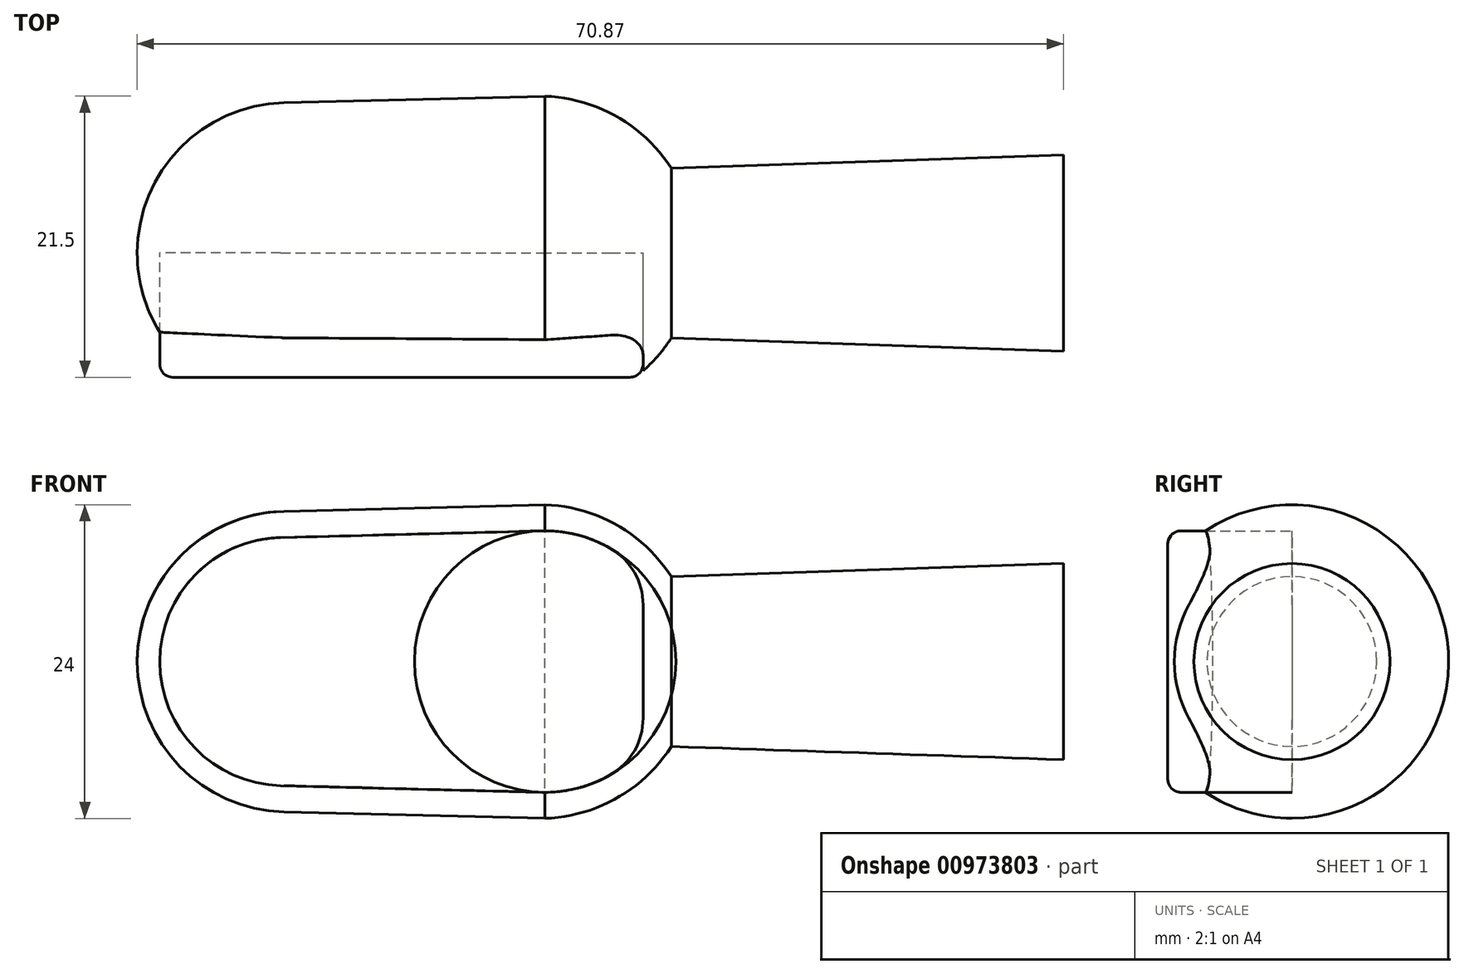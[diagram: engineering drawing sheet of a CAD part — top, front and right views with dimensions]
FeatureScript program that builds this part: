
annotation { "Feature Type Name" : "Feature", "Feature Type Description" : "" }
export const myFeature = defineFeature(function(context is Context, id is Id, definition is map)
    precondition{}
    {
        {
            var Q0;
            Q0=qCreatedBy(makeId("Right.planeOp"),FACE);
            var sketch = newSketch(context, id + "F0", { "sketchPlane" : qUnion([Q0])});
            skCircle(sketch, "E0", {"center": v(0, 0) * mm, "radius": 7.5 * mm});
            skSolve(sketch);
        }
        {
            var Q0;
            Q0=qCreatedBy(makeId("Right.planeOp"),FACE);
            cPlane(context, id + "F1", {"entities" : qUnion([Q0]), "cplaneType" : CPlaneType.OFFSET, "offset" : 30 * mm, "oppositeDirection" : true, "width" : 150 * mm, "height" : 150 * mm});
        }
        {
            var Q0;
            Q0=qCreatedBy(id+"F1.planeOp",FACE);
            var sketch = newSketch(context, id + "F2", { "sketchPlane" : qUnion([Q0])});
            skCircle(sketch, "E1", {"center": v(0, 0) * mm, "radius": 6.5 * mm});
            skSolve(sketch);
        }
        {
            var Q0;
            Q0=makeQuery(id+"F0.imprint","IMPRINT",FACE,{"disambiguationData":[TD([[makeQuery(id+"F0.imprint","IMPRINT",EDGE,{"derivedFrom":sQuery(id+"F0.wireOp",EDGE,"E0")}),1.0]])]});
            var Q1;
            Q1=makeQuery(id+"F2.imprint","IMPRINT",FACE,{"disambiguationData":[TD([[makeQuery(id+"F2.imprint","IMPRINT",EDGE,{"derivedFrom":sQuery(id+"F2.wireOp",EDGE,"E1")}),1.0]])]});
            loft(context, id + "F3", {"sheetProfilesArray" : [{ "sheetProfileEntities" : qUnion([Q0]) }, { "sheetProfileEntities" : qUnion([Q1]) }]});
        }
        {
            var Q0;
            Q0=qCreatedBy(makeId("Front.planeOp"),FACE);
            var sketch = newSketch(context, id + "F4", { "sketchPlane" : qUnion([Q0])});
            skLineSegment(sketch, "E2", {"start": v(0, 0) * mm, "end": v(-30, 0) * mm, "construction": true});
            skLineSegment(sketch, "E3", {"start": v(-30, 0) * mm, "end": v(-39.37, 0) * mm, "construction": true});
            skLineSegment(sketch, "E4", {"start": v(-39.37, 0) * mm, "end": v(-59.37, 0) * mm, "construction": true});
            skArc(sketch, "E5", {"start": v(-59.65, 11.5) * mm, "mid": v(-67.6, 8.03) * mm, "end": v(-70.87, 0) * mm});
            skLineSegment(sketch, "E6", {"start": v(-30, 0) * mm, "end": v(-30, 6.5) * mm});
            skPoint(sketch, "E7", {"position": v(-30, 6.5) * mm});
            skLineSegment(sketch, "E8", {"start": v(-59.65, 11.5) * mm, "end": v(-39.67, 12) * mm});
            skArc(sketch, "E9.trimOffspring", {"start": v(-30, 6.5) * mm, "mid": v(-34.16, 10.44) * mm, "end": v(-39.67, 12) * mm});
            skPoint(sketch, "E10", {"position": v(-30, -7.5) * mm});
            skLineSegment(sketch, "E11", {"start": v(-70.87, 0) * mm, "end": v(-30, 0) * mm});
            skPoint(sketch, "E12", {"position": v(-70.87, 0) * mm});
            skSolve(sketch);
        }
        {
            var Q0;
            Q0=makeQuery(id+"F4.imprint","IMPRINT",FACE,{"disambiguationData":[TD([[makeQuery(id+"F4.imprint","IMPRINT",EDGE,{"derivedFrom":sQuery(id+"F4.wireOp",EDGE,"E5")}),1.0]])]});
            var Q1;
            Q1=sQuery(id+"F4.wireOp",EDGE,"E4");
            revolve(context, id + "F5", {"operationType" : NewBodyOperationType.ADD, "surfaceOperationType" : NewSurfaceOperationType.NEW, "entities" : qUnion([Q0]), "axis" : qUnion([Q1]), "revolveType" : RevolveType.FULL});
        }
        {
            var Q0;
            Q0=qCreatedBy(makeId("Front.planeOp"),FACE);
            var sketch = newSketch(context, id + "F6", { "sketchPlane" : qUnion([Q0])});
            skLineSegment(sketch, "E13", {"start": v(0, 0) * mm, "end": v(-39.65, 0) * mm, "construction": true});
            skLineSegment(sketch, "E14", {"start": v(-39.65, 0) * mm, "end": v(-59.65, 0) * mm, "construction": true});
            skArc(sketch, "E15", {"start": v(-59.9, 9.49) * mm, "mid": v(-69.14, 0) * mm, "end": v(-59.9, -9.49) * mm});
            skArc(sketch, "E16", {"start": v(-39.9, -10) * mm, "mid": v(-37.19, -9.7) * mm, "end": v(-34.65, -8.66) * mm});
            skLineSegment(sketch, "E17", {"start": v(-59.9, 9.49) * mm, "end": v(-39.9, 10) * mm});
            skLineSegment(sketch, "E18", {"start": v(-39.9, -10) * mm, "end": v(-59.9, -9.49) * mm});
            skLineSegment(sketch, "E19", {"start": v(-32.15, 4.33) * mm, "end": v(-32.15, -4.33) * mm});
            skArc(sketch, "E20.trimOffspring", {"start": v(-34.65, 8.66) * mm, "mid": v(-37.19, 9.7) * mm, "end": v(-39.9, 10) * mm});
            skPoint(sketch, "E21.visualSharp", {"position": v(-32.15, 6.61) * mm});
            skArc(sketch, "E21.filletArc", {"start": v(-32.15, 4.33) * mm, "mid": v(-32.82, 6.83) * mm, "end": v(-34.65, 8.66) * mm});
            skPoint(sketch, "E22.visualSharp", {"position": v(-32.15, -6.61) * mm});
            skArc(sketch, "E22.filletArc", {"start": v(-34.65, -8.66) * mm, "mid": v(-32.82, -6.83) * mm, "end": v(-32.15, -4.33) * mm});
            skLineSegment(sketch, "E23", {"start": v(-39.67, 12) * mm, "end": v(-59.64, 11.49) * mm, "construction": true});
            skLineSegment(sketch, "E24", {"start": v(0, 0) * mm, "end": v(0, 12) * mm, "construction": true});
            skLineSegment(sketch, "E25", {"start": v(0, 12) * mm, "end": v(-39.67, 12) * mm, "construction": true});
            skSolve(sketch);
        }
        {
            var Q0;
            Q0 = qSketchRegion(id + "F6", true);
            extrude(context, id + "F7", {"entities" : qUnion([Q0]), "operationType" : NewBodyOperationType.REMOVE, "depth" : 15 * mm, "offsetDistance" : 25 * mm});
        }
        {
            var Q0;
            Q0=qCreatedBy(makeId("Front.planeOp"),FACE);
            var sketch = newSketch(context, id + "F8", { "sketchPlane" : qUnion([Q0])});
            skLineSegment(sketch, "E26", {"start": v(0, 0) * mm, "end": v(-39.65, 0) * mm, "construction": true});
            skLineSegment(sketch, "E27", {"start": v(-39.65, 0) * mm, "end": v(-59.65, 0) * mm, "construction": true});
            skArc(sketch, "E28", {"start": v(-59.9, 9.49) * mm, "mid": v(-69.14, 0) * mm, "end": v(-59.9, -9.49) * mm});
            skArc(sketch, "E29", {"start": v(-39.9, -10) * mm, "mid": v(-37.19, -9.7) * mm, "end": v(-34.65, -8.66) * mm});
            skLineSegment(sketch, "E30", {"start": v(-59.9, 9.49) * mm, "end": v(-39.9, 10) * mm});
            skLineSegment(sketch, "E31", {"start": v(-39.9, -10) * mm, "end": v(-59.9, -9.49) * mm});
            skLineSegment(sketch, "E32", {"start": v(-32.15, 4.33) * mm, "end": v(-32.15, -4.33) * mm});
            skArc(sketch, "E33.trimOffspring", {"start": v(-34.65, 8.66) * mm, "mid": v(-37.19, 9.7) * mm, "end": v(-39.9, 10) * mm});
            skPoint(sketch, "E34.visualSharp", {"position": v(-32.15, 6.61) * mm});
            skArc(sketch, "E34.filletArc", {"start": v(-32.15, 4.33) * mm, "mid": v(-32.82, 6.83) * mm, "end": v(-34.65, 8.66) * mm});
            skPoint(sketch, "E35.visualSharp", {"position": v(-32.15, -6.61) * mm});
            skArc(sketch, "E35.filletArc", {"start": v(-34.65, -8.66) * mm, "mid": v(-32.82, -6.83) * mm, "end": v(-32.15, -4.33) * mm});
            skLineSegment(sketch, "E36", {"start": v(-39.67, 12) * mm, "end": v(-59.64, 11.49) * mm, "construction": true});
            skLineSegment(sketch, "E37", {"start": v(0, 0) * mm, "end": v(0, 12) * mm, "construction": true});
            skLineSegment(sketch, "E38", {"start": v(0, 12) * mm, "end": v(-39.67, 12) * mm, "construction": true});
            skSolve(sketch);
        }
        {
            var Q0;
            Q0 = qSketchRegion(id + "F8", true);
            extrude(context, id + "F9", {"entities" : qUnion([Q0]), "depth" : 9.5 * mm, "offsetDistance" : 25 * mm});
        }
        {
            var Q0;
            Q0=makeQuery(id+"F9.opExtrude","CAP_EDGE",EDGE,{"disambiguationData":[OSD([sQuery(id+"F8.wireOp",EDGE,"E30")])],"isStart":false});
            fillet(context, id + "F10", {"entities" : qUnion([Q0]), "radius" : 1 * mm, "tangentPropagation" : true, "allowEdgeOverflow" : false});
        }
    });
